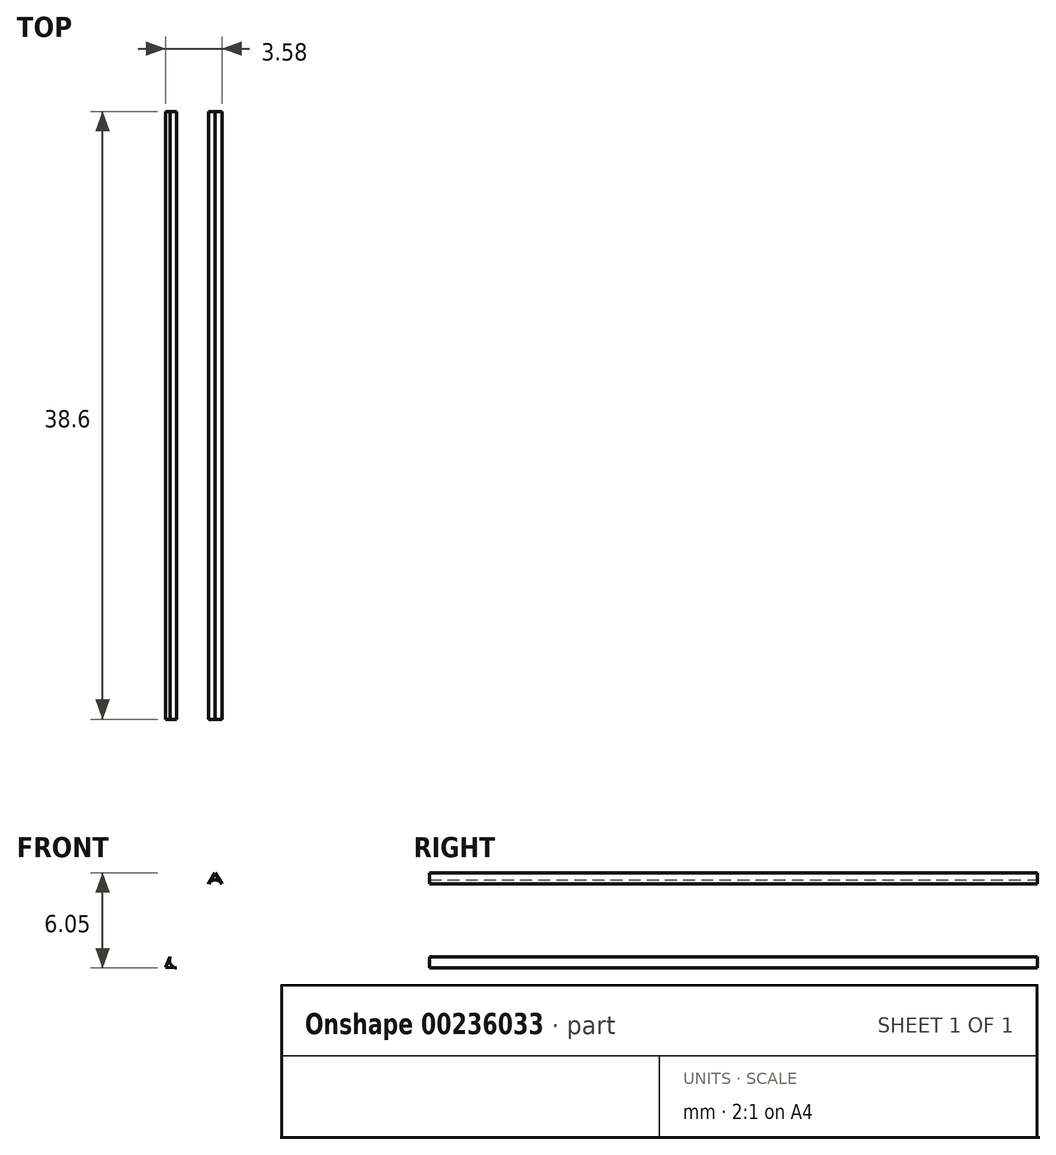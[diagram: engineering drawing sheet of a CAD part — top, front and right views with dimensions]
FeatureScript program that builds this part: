
annotation { "Feature Type Name" : "Feature", "Feature Type Description" : "" }
export const myFeature = defineFeature(function(context is Context, id is Id, definition is map)
    precondition{}
    {
        {
            var Q0;
            Q0=qCreatedBy(makeId("Front.planeOp"),FACE);
            var sketch = newSketch(context, id + "F0", { "sketchPlane" : qUnion([Q0])});
            skFitSpline(sketch, "E0", {"points": [v(0, 0) * mm, v(1.44, 3.07) * mm, v(3.15, 6) * mm], "startDerivative": vector(2.75, 6.2) * mm, "endDerivative": vector(3.55, 5.8) * mm});
            skFitSpline(sketch, "E1", {"points": [v(3.15, 6) * mm, v(4.86, 3.07) * mm, v(6.3, 0) * mm], "startDerivative": vector(3.55, -5.8) * mm, "endDerivative": vector(2.75, -6.2) * mm});
            skFitSpline(sketch, "E2", {"points": [v(6.3, 0) * mm, v(3.15, -0.15) * mm, v(0, 0) * mm], "startDerivative": vector(-6.3, -0.45) * mm, "endDerivative": vector(-6.3, 0.45) * mm});
            skArc(sketch, "E3.filletArc", {"start": v(3.58, 5.3) * mm, "mid": v(3.15, 5.54) * mm, "end": v(2.72, 5.3) * mm});
            skArc(sketch, "E4.filletArc", {"start": v(5.59, -0.05) * mm, "mid": v(5.98, 0.2) * mm, "end": v(6, 0.65) * mm});
            skArc(sketch, "E5.filletArc", {"start": v(0.3, 0.65) * mm, "mid": v(0.32, 0.2) * mm, "end": v(0.71, -0.05) * mm});
            skSolve(sketch);
        }
        {
            var Q0;
            Q0=makeQuery(id+"F0.imprint","IMPRINT",FACE,{"disambiguationData":[TD([[makeQuery(id+"F0.imprint","IMPRINT",EDGE,{"derivedFrom":sQuery(id+"F0.wireOp",EDGE,"E0")}),-1.0]])]});
            extrude(context, id + "F1", {"entities" : qUnion([Q0]), "depth" : 38.6 * mm});
        }
    });
